# Revit family: BE_77150_de_DE
name_source: partatom
category: Leuchten
revit_build: Autodesk Revit 2015 (Build: 20150704_0715(x64)
units: mm (PartAtom-declared; Revit-internal decimal feet)

## types (4) — shared parameters
AC/DC = AC/DC
Aktualisierung = 2015-12-09T04:08:32
BEGA_Dummy = Nein
BEGA_IES = Ja
BEGA_Intern = Ja
BEGA_Intern_Konstruktion = Ja
BEGA_Intern_an = Ja
BEGA_Intern_aus = Ja
Beschreibung = Aufsatzleuchte
Beschreibung_Sonderanfertigung = Hier können Sie Informationen zur Sonderanfertigung eintragen.
CE_Konformität = ja
Einstecktiefe = 60 mm
Energieeffizienzklasse = LED A++ - A
Farbfilter = 16777215
Farbtemperaturverschiebung bei Dämpfen der Lampe = <Keine Auswahl>
Farbwiedergabeindex = Ra > 80
Frequenz = 0/50-60 Hz
Gewicht = 5.95 kg
Hersteller = BEGA
Lampe = LED 16 W
Lastklassifizierung = Beleuchtung
Lebensdauerkriterien = L70 = 50.000 h
Logo = BEGA_Logo.png
Material_02 = BEGA_Oberfläche_Silber_matt
Material_06 = BEGA_Oberfläche_Edelstahl_gebürstet
Material_12 = BEGA_Kunststoff_klar
Material_13 = BEGA_Kunststoff_matt
Material_15 = BEGA_Leuchtmedium_matt
Material_17 = BEGA_Reflektor
Material_19 = BEGA_Dummy_matt
Neigungswinkel = 0.00°
Produktdatenblatt = http://www.bega.de
Scheinlast = 0 VA
Schutzart = IP 65
Schutzklasse = II
Sonderanfertigung = Nein
Spannung = 0 V
Typenbild = 77150.png
URL = http://www.bega.de
Windangriffsfläche = 0.15 m²
zero-valued in all types: Vorgabe-Ansicht

## per-type parameters (varying)
| type | Bestellnummer | Datei für fotometrisches Netz | Farbtemperatur | LED_Modulbezeichnung | Lampenlichtstrom | Leuchtenlichtstrom | M_A | M_G | Modell |
| BEGA_77150_Grafit_K4 | 77150 | BE_77150.IES | 4000 K | LED-0553/840 + LED-0554/840 | 2520 lm | 1397 lm | Nein | Ja | 77150 |
| BEGA_77150_Silber_K3 | 77150AK3 | BE_77150K3.IES | 3000 K | LED-0553/830 + LED-0554/830 | 2360 lm | 1308 lm | Ja | Nein | 77150AK3 |
| BEGA_77150_Grafit_K3 | 77150K3 | BE_77150K3.IES | 3000 K | LED-0553/830 + LED-0554/830 | 2360 lm | 1308 lm | Nein | Ja | 77150K3 |
| BEGA_77150_Silber_K4 | 77150A | BE_77150.IES | 4000 K | LED-0553/840 + LED-0554/840 | 2520 lm | 1397 lm | Ja | Nein | 77150A |
